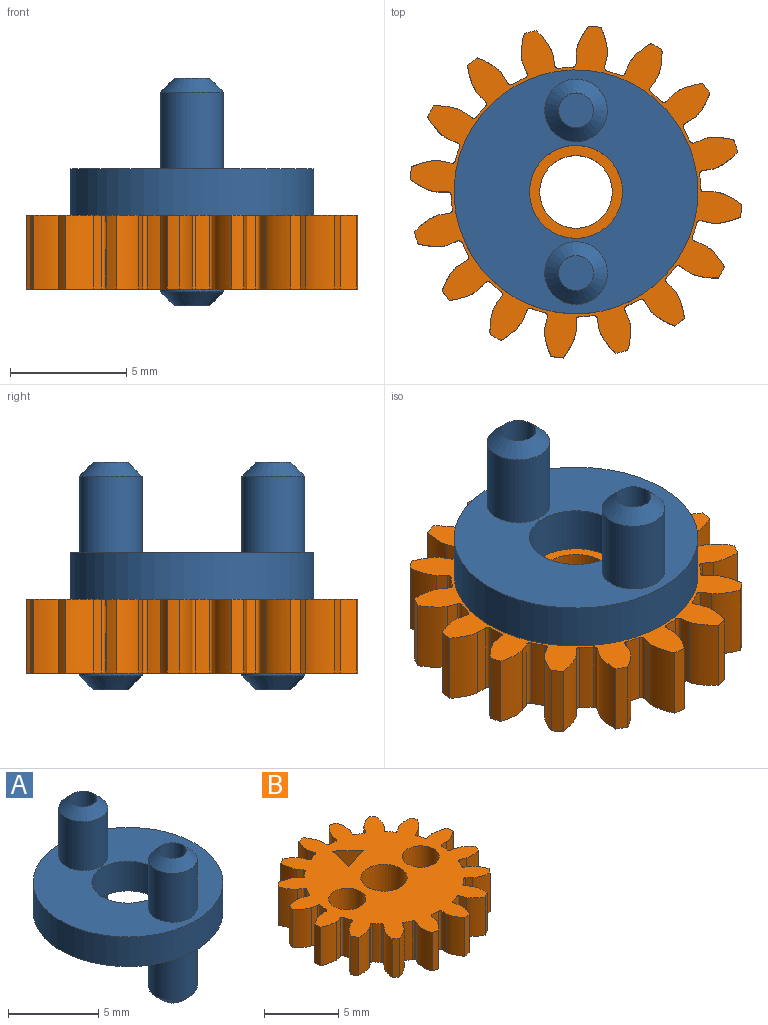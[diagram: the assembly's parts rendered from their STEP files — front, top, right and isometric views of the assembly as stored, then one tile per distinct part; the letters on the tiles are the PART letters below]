
ASSEMBLY  parts=2 mates=1
PART A: 20 faces, bbox 10.5x10.5x9.8 mm
  f0: cylinder r=5.25mm len=10.5mm, axis (0,0,-1), area 66mm2, adj f1,f11
  f1: plane 10.5x10.5mm, normal (0,0,1), area 62.6mm2, adj f0,f2,f3,f4
  f2: cylinder r=2mm len=4mm, axis (0,0,1), area 25.1mm2, adj f1,f11
  f3: cylinder r=1.35mm len=3.3mm, axis (0,0,-1), area 28mm2, adj f1,f10
  f4: cylinder r=1.35mm len=3.3mm, axis (0,0,-1), area 28mm2, adj f1,f9
  f5: cylinder r=0.75mm len=3.9mm, axis (0,0,1), area 18.4mm2, adj f6,f9
  f6: plane 1.5x1.5mm, normal (0,0,1), area 1.8mm2, adj f5
  f7: cylinder r=0.75mm len=3.9mm, axis (0,0,1), area 18.4mm2, adj f8,f10
  f8: plane 1.5x1.5mm, normal (0,0,1), area 1.8mm2, adj f7
  f9: cone r=1.35mm half-angle=45deg, axis (0,0,-1), area 5.6mm2, adj f4,f5
  f10: cone r=0.65mm half-angle=45deg, axis (0,0,-1), area 5.6mm2, adj f3,f7
  f11: plane 10.5x10.5mm, normal (0,0,-1), area 62.6mm2, adj f0,f2,f12,f13
  f12: cylinder r=1.35mm len=3.3mm, axis (0,0,1), area 28mm2, adj f11,f19
  f13: cylinder r=1.35mm len=3.3mm, axis (0,0,1), area 28mm2, adj f11,f18
  f14: cylinder r=0.75mm len=3.9mm, axis (0,0,-1), area 18.4mm2, adj f15,f18
  f15: plane 1.5x1.5mm, normal (0,0,-1), area 1.8mm2, adj f14
  f16: cylinder r=0.75mm len=3.9mm, axis (0,0,-1), area 18.4mm2, adj f17,f19
  f17: plane 1.5x1.5mm, normal (0,0,-1), area 1.8mm2, adj f16
  f18: cone r=1.35mm half-angle=45deg, axis (0,0,1), area 5.6mm2, adj f13,f14
  f19: cone r=0.65mm half-angle=45deg, axis (0,0,1), area 5.6mm2, adj f12,f16
PART B: 136 faces, bbox 14.3x14.3x3.2 mm
  f0: plane 14.28x14.28mm, normal (0,0,1), area 104mm2, adj f2,f3,f4,f5,f6,f7,f8,f9
  f1: plane 14.28x14.28mm, normal (0,0,-1), area 104mm2, adj f2,f3,f4,f5,f6,f7,f8,f9
  f2: cylinder r=7.16mm len=3.18mm, axis (0,0,-1), area 1.7mm2, adj f0,f1,f6,f13
  f3: cylinder r=0.15mm len=3.18mm, axis (0,0,1), area 0.7mm2, adj f0,f1,f7,f9
  f4: cylinder r=0.15mm len=3.18mm, axis (0,0,1), area 0.7mm2, adj f0,f1,f7,f8
  f5: extruded ~3.18x1.25mm, area 4.1mm2, adj f0,f1,f9,f122
  f6: extruded ~3.18x0.95mm, area 4.1mm2, adj f0,f1,f2,f8
  f7: cylinder r=5.37mm len=3.18mm, axis (0,0,1), area 1.9mm2, adj f0,f1,f3,f4
  f8: plane 3.18x0.43mm, normal (0.38,-0.92,0), area 1.5mm2, adj f0,f1,f4,f6
  f9: plane 3.18x0.45mm, normal (-0.22,0.97,0), area 1.5mm2, adj f0,f1,f3,f5
  f10: cylinder r=7.16mm len=3.18mm, axis (0,0,-1), area 1.7mm2, adj f0,f1,f14,f21
  f11: cylinder r=0.15mm len=3.18mm, axis (0,0,1), area 0.7mm2, adj f0,f1,f15,f17
  f12: cylinder r=0.15mm len=3.18mm, axis (0,0,1), area 0.7mm2, adj f0,f1,f15,f16
  f13: extruded ~3.18x1.26mm, area 4.1mm2, adj f0,f1,f2,f17
  f14: extruded ~3.18x1.2mm, area 4.1mm2, adj f0,f1,f10,f16
  f15: cylinder r=5.37mm len=3.18mm, axis (0,0,1), area 1.9mm2, adj f0,f1,f11,f12
  f16: plane 3.18x0.33mm, normal (0.71,-0.71,0), area 1.5mm2, adj f0,f1,f12,f14
  f17: plane 3.18x0.38mm, normal (-0.58,0.81,0), area 1.5mm2, adj f0,f1,f11,f13
  f18: cylinder r=7.16mm len=3.18mm, axis (0,0,-1), area 1.7mm2, adj f0,f1,f22,f29
  f19: cylinder r=0.15mm len=3.18mm, axis (0,0,1), area 0.7mm2, adj f0,f1,f23,f25
  f20: cylinder r=0.15mm len=3.18mm, axis (0,0,1), area 0.7mm2, adj f0,f1,f23,f24
  f21: extruded ~3.18x1.08mm, area 4.1mm2, adj f0,f1,f10,f25
  f22: extruded ~3.18x1.28mm, area 4.1mm2, adj f0,f1,f18,f24
  f23: cylinder r=5.37mm len=3.18mm, axis (0,0,1), area 1.9mm2, adj f0,f1,f19,f20
  f24: plane 3.18x0.43mm, normal (0.92,-0.38,0), area 1.5mm2, adj f0,f1,f20,f22
  f25: plane 3.18x0.39mm, normal (-0.85,0.53,0), area 1.5mm2, adj f0,f1,f19,f21
  f26: cylinder r=7.16mm len=3.18mm, axis (0,0,-1), area 1.7mm2, adj f0,f1,f30,f37
  f27: cylinder r=0.15mm len=3.18mm, axis (0,0,1), area 0.7mm2, adj f0,f1,f31,f33
  f28: cylinder r=0.15mm len=3.18mm, axis (0,0,1), area 0.7mm2, adj f0,f1,f31,f32
  f29: extruded ~3.18x1.05mm, area 4.1mm2, adj f0,f1,f18,f33
  f30: extruded ~3.18x1.16mm, area 4.1mm2, adj f0,f1,f26,f32
  f31: cylinder r=5.37mm len=3.18mm, axis (0,0,1), area 1.9mm2, adj f0,f1,f27,f28
  f32: plane 3.18x0.46mm, normal (1,0,0), area 1.5mm2, adj f0,f1,f28,f30
  f33: plane 3.18x0.46mm, normal (-0.99,0.17,0), area 1.5mm2, adj f0,f1,f27,f29
  f34: cylinder r=7.16mm len=3.18mm, axis (0,0,-1), area 1.7mm2, adj f0,f1,f38,f45
  f35: cylinder r=0.15mm len=3.18mm, axis (0,0,1), area 0.7mm2, adj f0,f1,f39,f41
  f36: cylinder r=0.15mm len=3.18mm, axis (0,0,1), area 0.7mm2, adj f0,f1,f39,f40
  f37: extruded ~3.18x1.25mm, area 4.1mm2, adj f0,f1,f26,f41
  f38: extruded ~3.18x0.95mm, area 4.1mm2, adj f0,f1,f34,f40
  f39: cylinder r=5.37mm len=3.18mm, axis (0,0,1), area 1.9mm2, adj f0,f1,f35,f36
  f40: plane 3.18x0.43mm, normal (0.92,0.38,0), area 1.5mm2, adj f0,f1,f36,f38
  f41: plane 3.18x0.45mm, normal (-0.97,-0.22,0), area 1.5mm2, adj f0,f1,f35,f37
  f42: cylinder r=7.16mm len=3.18mm, axis (0,0,-1), area 1.7mm2, adj f0,f1,f46,f53
  f43: cylinder r=0.15mm len=3.18mm, axis (0,0,1), area 0.7mm2, adj f0,f1,f47,f49
  f44: cylinder r=0.15mm len=3.18mm, axis (0,0,1), area 0.7mm2, adj f0,f1,f47,f48
  f45: extruded ~3.18x1.26mm, area 4.1mm2, adj f0,f1,f34,f49
  f46: extruded ~3.18x1.2mm, area 4.1mm2, adj f0,f1,f42,f48
  f47: cylinder r=5.37mm len=3.18mm, axis (0,0,1), area 1.9mm2, adj f0,f1,f43,f44
  f48: plane 3.18x0.33mm, normal (0.71,0.71,0), area 1.5mm2, adj f0,f1,f44,f46
  f49: plane 3.18x0.38mm, normal (-0.81,-0.58,0), area 1.5mm2, adj f0,f1,f43,f45
  f50: cylinder r=7.16mm len=3.18mm, axis (0,0,-1), area 1.7mm2, adj f0,f1,f54,f61
  f51: cylinder r=0.15mm len=3.18mm, axis (0,0,1), area 0.7mm2, adj f0,f1,f55,f57
  f52: cylinder r=0.15mm len=3.18mm, axis (0,0,1), area 0.7mm2, adj f0,f1,f55,f56
  f53: extruded ~3.18x1.08mm, area 4.1mm2, adj f0,f1,f42,f57
  f54: extruded ~3.18x1.28mm, area 4.1mm2, adj f0,f1,f50,f56
  f55: cylinder r=5.37mm len=3.18mm, axis (0,0,1), area 1.9mm2, adj f0,f1,f51,f52
  f56: plane 3.18x0.43mm, normal (0.38,0.92,0), area 1.5mm2, adj f0,f1,f52,f54
  f57: plane 3.18x0.39mm, normal (-0.53,-0.85,0), area 1.5mm2, adj f0,f1,f51,f53
  f58: cylinder r=7.16mm len=3.18mm, axis (0,0,-1), area 1.7mm2, adj f0,f1,f62,f69
  f59: cylinder r=0.15mm len=3.18mm, axis (0,0,1), area 0.7mm2, adj f0,f1,f63,f65
  f60: cylinder r=0.15mm len=3.18mm, axis (0,0,1), area 0.7mm2, adj f0,f1,f63,f64
  f61: extruded ~3.18x1.05mm, area 4.1mm2, adj f0,f1,f50,f65
  f62: extruded ~3.18x1.16mm, area 4.1mm2, adj f0,f1,f58,f64
  f63: cylinder r=5.37mm len=3.18mm, axis (0,0,1), area 1.9mm2, adj f0,f1,f59,f60
  f64: plane 3.18x0.46mm, normal (0,1,0), area 1.5mm2, adj f0,f1,f60,f62
  f65: plane 3.18x0.46mm, normal (-0.17,-0.99,0), area 1.5mm2, adj f0,f1,f59,f61
  f66: cylinder r=7.16mm len=3.18mm, axis (0,0,-1), area 1.7mm2, adj f0,f1,f70,f77
  f67: cylinder r=0.15mm len=3.18mm, axis (0,0,1), area 0.7mm2, adj f0,f1,f71,f73
  f68: cylinder r=0.15mm len=3.18mm, axis (0,0,1), area 0.7mm2, adj f0,f1,f71,f72
  f69: extruded ~3.18x1.25mm, area 4.1mm2, adj f0,f1,f58,f73
  f70: extruded ~3.18x0.95mm, area 4.1mm2, adj f0,f1,f66,f72
  f71: cylinder r=5.37mm len=3.18mm, axis (0,0,1), area 1.9mm2, adj f0,f1,f67,f68
  f72: plane 3.18x0.43mm, normal (-0.38,0.92,0), area 1.5mm2, adj f0,f1,f68,f70
  f73: plane 3.18x0.45mm, normal (0.22,-0.97,0), area 1.5mm2, adj f0,f1,f67,f69
  f74: cylinder r=7.16mm len=3.18mm, axis (0,0,-1), area 1.7mm2, adj f0,f1,f78,f85
  f75: cylinder r=0.15mm len=3.18mm, axis (0,0,1), area 0.7mm2, adj f0,f1,f79,f81
  f76: cylinder r=0.15mm len=3.18mm, axis (0,0,1), area 0.7mm2, adj f0,f1,f79,f80
  f77: extruded ~3.18x1.26mm, area 4.1mm2, adj f0,f1,f66,f81
  f78: extruded ~3.18x1.2mm, area 4.1mm2, adj f0,f1,f74,f80
  f79: cylinder r=5.37mm len=3.18mm, axis (0,0,1), area 1.9mm2, adj f0,f1,f75,f76
  f80: plane 3.18x0.33mm, normal (-0.71,0.71,0), area 1.5mm2, adj f0,f1,f76,f78
  f81: plane 3.18x0.38mm, normal (0.58,-0.81,0), area 1.5mm2, adj f0,f1,f75,f77
  f82: cylinder r=7.16mm len=3.18mm, axis (0,0,-1), area 1.7mm2, adj f0,f1,f86,f93
  f83: cylinder r=0.15mm len=3.18mm, axis (0,0,1), area 0.7mm2, adj f0,f1,f87,f89
  f84: cylinder r=0.15mm len=3.18mm, axis (0,0,1), area 0.7mm2, adj f0,f1,f87,f88
  f85: extruded ~3.18x1.08mm, area 4.1mm2, adj f0,f1,f74,f89
  f86: extruded ~3.18x1.28mm, area 4.1mm2, adj f0,f1,f82,f88
  f87: cylinder r=5.37mm len=3.18mm, axis (0,0,1), area 1.9mm2, adj f0,f1,f83,f84
  f88: plane 3.18x0.43mm, normal (-0.92,0.38,0), area 1.5mm2, adj f0,f1,f84,f86
  f89: plane 3.18x0.39mm, normal (0.85,-0.53,0), area 1.5mm2, adj f0,f1,f83,f85
  f90: cylinder r=7.16mm len=3.18mm, axis (0,0,-1), area 1.7mm2, adj f0,f1,f94,f101
  f91: cylinder r=0.15mm len=3.18mm, axis (0,0,1), area 0.7mm2, adj f0,f1,f95,f97
  f92: cylinder r=0.15mm len=3.18mm, axis (0,0,1), area 0.7mm2, adj f0,f1,f95,f96
  f93: extruded ~3.18x1.05mm, area 4.1mm2, adj f0,f1,f82,f97
  f94: extruded ~3.18x1.16mm, area 4.1mm2, adj f0,f1,f90,f96
  f95: cylinder r=5.37mm len=3.18mm, axis (0,0,1), area 1.9mm2, adj f0,f1,f91,f92
  f96: plane 3.18x0.46mm, normal (-1,0,0), area 1.5mm2, adj f0,f1,f92,f94
  f97: plane 3.18x0.46mm, normal (0.99,-0.17,0), area 1.5mm2, adj f0,f1,f91,f93
  f98: cylinder r=7.16mm len=3.18mm, axis (0,0,-1), area 1.7mm2, adj f0,f1,f102,f109
  f99: cylinder r=0.15mm len=3.18mm, axis (0,0,1), area 0.7mm2, adj f0,f1,f103,f105
  f100: cylinder r=0.15mm len=3.18mm, axis (0,0,1), area 0.7mm2, adj f0,f1,f103,f104
  f101: extruded ~3.18x1.25mm, area 4.1mm2, adj f0,f1,f90,f105
  f102: extruded ~3.18x0.95mm, area 4.1mm2, adj f0,f1,f98,f104
  f103: cylinder r=5.37mm len=3.18mm, axis (0,0,1), area 1.9mm2, adj f0,f1,f99,f100
  f104: plane 3.18x0.43mm, normal (-0.92,-0.38,0), area 1.5mm2, adj f0,f1,f100,f102
  f105: plane 3.18x0.45mm, normal (0.97,0.22,0), area 1.5mm2, adj f0,f1,f99,f101
  f106: cylinder r=7.16mm len=3.18mm, axis (0,0,-1), area 1.7mm2, adj f0,f1,f110,f117
  f107: cylinder r=0.15mm len=3.18mm, axis (0,0,1), area 0.7mm2, adj f0,f1,f111,f113
  f108: cylinder r=0.15mm len=3.18mm, axis (0,0,1), area 0.7mm2, adj f0,f1,f111,f112
  f109: extruded ~3.18x1.26mm, area 4.1mm2, adj f0,f1,f98,f113
  f110: extruded ~3.18x1.2mm, area 4.1mm2, adj f0,f1,f106,f112
  f111: cylinder r=5.37mm len=3.18mm, axis (0,0,1), area 1.9mm2, adj f0,f1,f107,f108
  f112: plane 3.18x0.33mm, normal (-0.71,-0.71,0), area 1.5mm2, adj f0,f1,f108,f110
  f113: plane 3.18x0.38mm, normal (0.81,0.58,0), area 1.5mm2, adj f0,f1,f107,f109
  f114: cylinder r=7.16mm len=3.18mm, axis (0,0,-1), area 1.7mm2, adj f0,f1,f118,f127
  f115: cylinder r=0.15mm len=3.18mm, axis (0,0,1), area 0.7mm2, adj f0,f1,f119,f121
  f116: cylinder r=0.15mm len=3.18mm, axis (0,0,1), area 0.7mm2, adj f0,f1,f119,f120
  f117: extruded ~3.18x1.08mm, area 4.1mm2, adj f0,f1,f106,f121
  f118: extruded ~3.18x1.28mm, area 4.1mm2, adj f0,f1,f114,f120
  f119: cylinder r=5.37mm len=3.18mm, axis (0,0,1), area 1.9mm2, adj f0,f1,f115,f116
  f120: plane 3.18x0.43mm, normal (-0.38,-0.92,0), area 1.5mm2, adj f0,f1,f116,f118
  f121: plane 3.18x0.39mm, normal (0.53,0.85,0), area 1.5mm2, adj f0,f1,f115,f117
  f122: cylinder r=7.16mm len=3.18mm, axis (0,0,-1), area 1.7mm2, adj f0,f1,f5,f123
  f123: extruded ~3.18x1.16mm, area 4.1mm2, adj f0,f1,f122,f124
  f124: plane 3.18x0.46mm, normal (0,-1,0), area 1.5mm2, adj f0,f1,f123,f128
  f125: cylinder r=5.37mm len=3.18mm, axis (0,0,1), area 1.9mm2, adj f0,f1,f128,f129
  f126: plane 3.18x0.46mm, normal (0.17,0.99,0), area 1.5mm2, adj f0,f1,f127,f129
  f127: extruded ~3.18x1.05mm, area 4.1mm2, adj f0,f1,f114,f126
  f128: cylinder r=0.15mm len=3.18mm, axis (0,0,1), area 0.7mm2, adj f0,f1,f124,f125
  f129: cylinder r=0.15mm len=3.18mm, axis (0,0,1), area 0.7mm2, adj f0,f1,f125,f126
  f130: cylinder r=1.56mm len=3.18mm, axis (0,0,1), area 31.2mm2, adj f0,f1
  f131: cylinder r=1.25mm len=3.18mm, axis (0,0,1), area 24.9mm2, adj f0,f1
  f132: cylinder r=1.25mm len=3.18mm, axis (0,0,1), area 24.9mm2, adj f0,f1
  f133: plane 3.18x1.51mm, normal (-0.69,-0.72,0), area 6.6mm2, adj f0,f1,f134,f135
  f134: plane 3.18x2.03mm, normal (0.97,-0.24,0), area 6.6mm2, adj f0,f1,f133,f135
  f135: plane 3.18x2mm, normal (-0.28,0.96,0), area 6.6mm2, adj f0,f1,f133,f134
PLACE A at identity fixed
PLACE B rot(axis=(0.71,-0.71,0),180deg) t=(0,0,-2.59)mm
MATE fastened B.f7 <-> A.f2  axis (0,0,1) through (0,0,-1)mm
